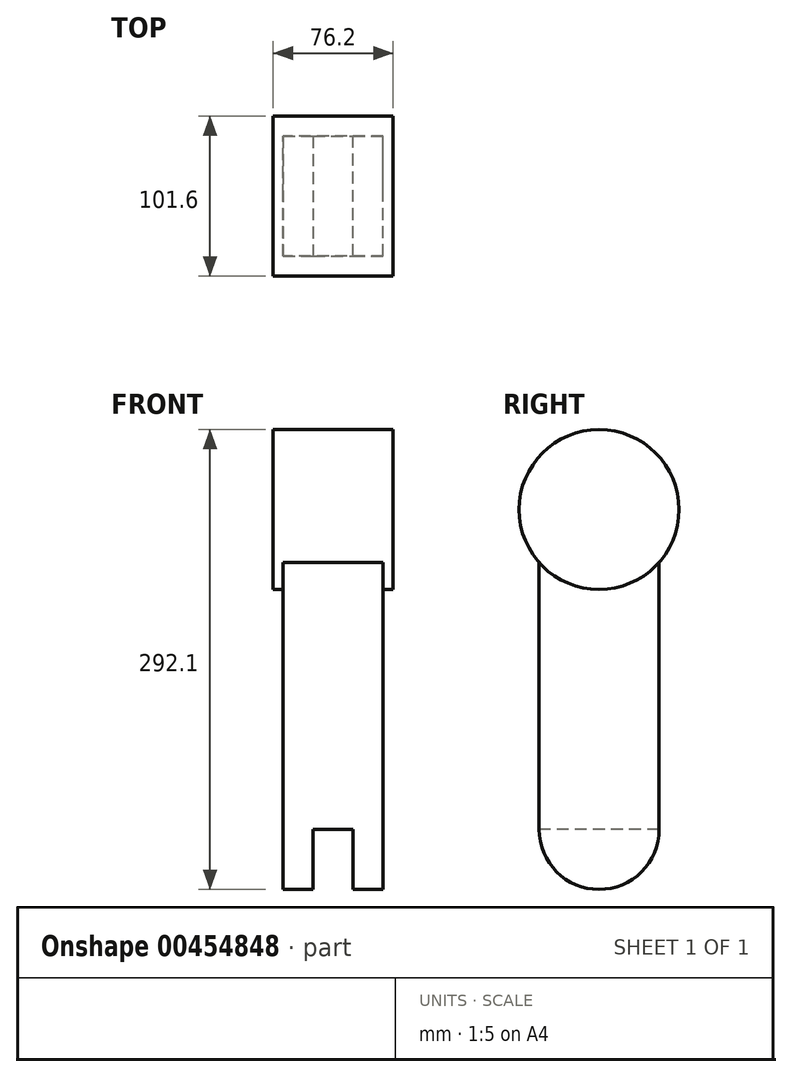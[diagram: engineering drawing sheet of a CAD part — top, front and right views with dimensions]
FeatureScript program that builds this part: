
annotation { "Feature Type Name" : "Feature", "Feature Type Description" : "" }
export const myFeature = defineFeature(function(context is Context, id is Id, definition is map)
    precondition{}
    {
        {
            var Q0;
            Q0=qCreatedBy(makeId("Right.planeOp"),FACE);
            var sketch = newSketch(context, id + "F0", { "sketchPlane" : qUnion([Q0])});
            skCircle(sketch, "E0", {"center": v(0, 0) * mm, "radius": 50.8 * mm});
            skSolve(sketch);
        }
        {
            var Q0;
            Q0 = qSketchRegion(id + "F0", true);
            extrude(context, id + "F1", {"entities" : qUnion([Q0]), "endBound" : BoundingType.SYMMETRIC, "depth" : 76.2 * mm, "offsetDistance" : 25.4 * mm});
        }
        {
            var Q0;
            Q0=qCreatedBy(makeId("Top.planeOp"),FACE);
            var sketch = newSketch(context, id + "F2", { "sketchPlane" : qUnion([Q0])});
            skLineSegment(sketch, "E1.bottom", {"start": v(-31.75, -38.1) * mm, "end": v(31.75, -38.1) * mm});
            skLineSegment(sketch, "E1.top", {"start": v(-31.75, 38.1) * mm, "end": v(31.75, 38.1) * mm});
            skLineSegment(sketch, "E1.left", {"start": v(-31.75, -38.1) * mm, "end": v(-31.75, 38.1) * mm});
            skLineSegment(sketch, "E1.right", {"start": v(31.75, -38.1) * mm, "end": v(31.75, 38.1) * mm});
            skPoint(sketch, "E1.middle", {"position": v(0, 0) * mm});
            skSolve(sketch);
        }
        {
            var Q0;
            Q0 = qSketchRegion(id + "F2", true);
            extrude(context, id + "F3", {"entities" : qUnion([Q0]), "operationType" : NewBodyOperationType.ADD, "oppositeDirection" : true, "depth" : 203.2 * mm, "offsetDistance" : 25.4 * mm});
        }
        {
            var Q0;
            Q0=makeQuery(id+"F3.opExtrude","SWEPT_FACE",FACE,{"disambiguationData":[OSD([sQuery(id+"F2.wireOp",EDGE,"E1.right")])]});
            var sketch = newSketch(context, id + "F4", { "sketchPlane" : qUnion([Q0])});
            skCircle(sketch, "E2", {"center": v(0, -203.2) * mm, "radius": 38.1 * mm});
            skSolve(sketch);
        }
        {
            var Q0;
            Q0 = qSketchRegion(id + "F4", true);
            extrude(context, id + "F5", {"entities" : qUnion([Q0]), "operationType" : NewBodyOperationType.ADD, "oppositeDirection" : true, "depth" : 19.05 * mm, "offsetDistance" : 25.4 * mm});
        }
        {
            var Q0;
            Q0=makeQuery(id+"F3.opExtrude","SWEPT_FACE",FACE,{"disambiguationData":[OSD([sQuery(id+"F2.wireOp",EDGE,"E1.left")])]});
            var sketch = newSketch(context, id + "F6", { "sketchPlane" : qUnion([Q0])});
            skCircle(sketch, "E3", {"center": v(0, -203.2) * mm, "radius": 38.1 * mm});
            skSolve(sketch);
        }
        {
            var Q0;
            Q0 = qSketchRegion(id + "F6", true);
            extrude(context, id + "F7", {"entities" : qUnion([Q0]), "operationType" : NewBodyOperationType.ADD, "oppositeDirection" : true, "depth" : 19.05 * mm, "offsetDistance" : 25.4 * mm});
        }
    });
